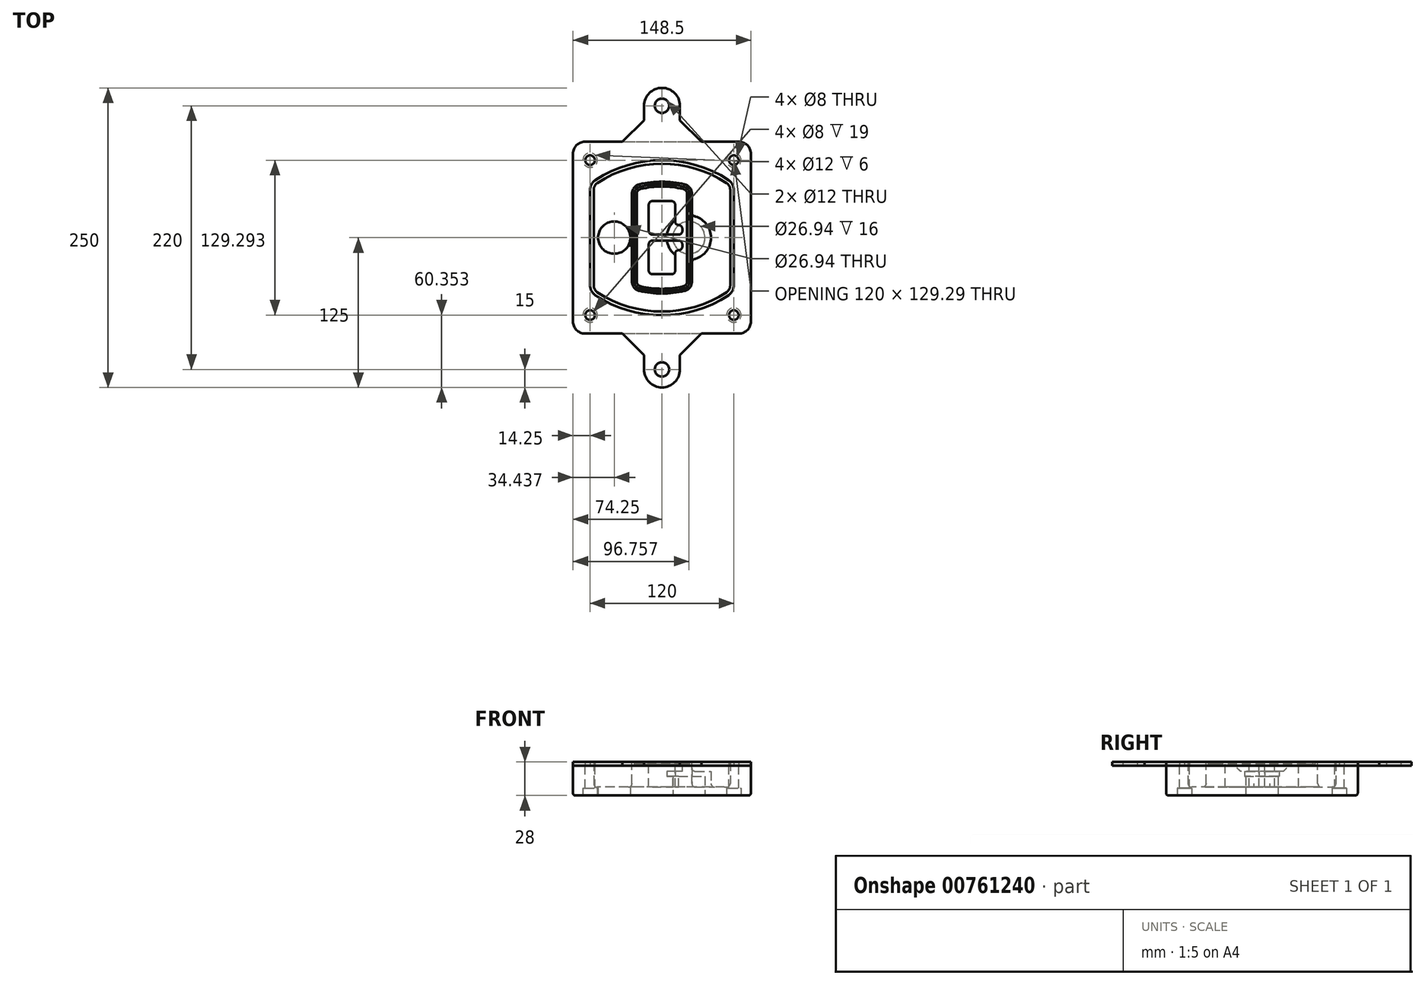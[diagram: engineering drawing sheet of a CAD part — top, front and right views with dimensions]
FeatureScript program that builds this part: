
annotation { "Feature Type Name" : "Feature", "Feature Type Description" : "" }
export const myFeature = defineFeature(function(context is Context, id is Id, definition is map)
    precondition{}
    {
        {
            var Q0;
            Q0=qCreatedBy(makeId("Top.planeOp"),FACE);
            var sketch = newSketch(context, id + "F0", { "sketchPlane" : qUnion([Q0])});
            skPoint(sketch, "E0.rect.middle", {"position": v(0, 0) * mm});
            skLineSegment(sketch, "E1.bottom", {"start": v(-64.25, -80) * mm, "end": v(64.25, -80) * mm});
            skLineSegment(sketch, "E1.top", {"start": v(-64.25, 80) * mm, "end": v(64.25, 80) * mm});
            skLineSegment(sketch, "E1.left", {"start": v(-74.25, -70) * mm, "end": v(-74.25, 70) * mm});
            skLineSegment(sketch, "E1.right", {"start": v(74.25, -70) * mm, "end": v(74.25, 70) * mm});
            skLineSegment(sketch, "E2", {"start": v(-74.25, 80) * mm, "end": v(74.25, -80) * mm, "construction": true});
            skLineSegment(sketch, "E3", {"start": v(74.25, 80) * mm, "end": v(-74.25, -80) * mm, "construction": true});
            skCircle(sketch, "E4", {"center": v(-60, 64.65) * mm, "radius": 4 * mm});
            skCircle(sketch, "E5", {"center": v(60, 64.65) * mm, "radius": 4 * mm});
            skCircle(sketch, "E6", {"center": v(60, -64.65) * mm, "radius": 4 * mm});
            skCircle(sketch, "E7", {"center": v(-60, -64.65) * mm, "radius": 4 * mm});
            skLineSegment(sketch, "E8", {"start": v(-60, 64.65) * mm, "end": v(60, 64.65) * mm, "construction": true});
            skLineSegment(sketch, "E9", {"start": v(60, 64.65) * mm, "end": v(60, -64.65) * mm, "construction": true});
            skLineSegment(sketch, "E10", {"start": v(60, -64.65) * mm, "end": v(-60, -64.65) * mm, "construction": true});
            skLineSegment(sketch, "E11", {"start": v(-60, -64.65) * mm, "end": v(-60, 64.65) * mm, "construction": true});
            skLineSegment(sketch, "E12", {"start": v(-60, 39.77) * mm, "end": v(-60, -39.77) * mm});
            skLineSegment(sketch, "E13", {"start": v(60, 39.77) * mm, "end": v(60, -39.77) * mm});
            skArc(sketch, "E14", {"start": v(55.47, 48.14) * mm, "mid": v(0, 64.65) * mm, "end": v(-55.47, 48.14) * mm});
            skArc(sketch, "E15", {"start": v(-55.47, -48.14) * mm, "mid": v(0, -64.65) * mm, "end": v(55.47, -48.14) * mm});
            skLineSegment(sketch, "E16", {"start": v(-60, 0) * mm, "end": v(60, 0) * mm, "construction": true});
            skPoint(sketch, "E17.visualSharp", {"position": v(-60, -45) * mm});
            skArc(sketch, "E17.filletArc", {"start": v(-60, -39.77) * mm, "mid": v(-58.8, -44.53) * mm, "end": v(-55.47, -48.14) * mm});
            skPoint(sketch, "E18.visualSharp", {"position": v(-60, 45) * mm});
            skArc(sketch, "E18.filletArc", {"start": v(-55.47, 48.14) * mm, "mid": v(-58.8, 44.53) * mm, "end": v(-60, 39.77) * mm});
            skPoint(sketch, "E19.visualSharp", {"position": v(60, 45) * mm});
            skArc(sketch, "E19.filletArc", {"start": v(60, 39.77) * mm, "mid": v(58.8, 44.53) * mm, "end": v(55.47, 48.14) * mm});
            skPoint(sketch, "E20.visualSharp", {"position": v(60, -45) * mm});
            skArc(sketch, "E20.filletArc", {"start": v(55.47, -48.14) * mm, "mid": v(58.8, -44.53) * mm, "end": v(60, -39.77) * mm});
            skPoint(sketch, "E21.visualSharp", {"position": v(-74.25, 80) * mm});
            skArc(sketch, "E21.filletArc", {"start": v(-64.25, 80) * mm, "mid": v(-71.32, 77.07) * mm, "end": v(-74.25, 70) * mm});
            skPoint(sketch, "E22.visualSharp", {"position": v(74.25, 80) * mm});
            skArc(sketch, "E22.filletArc", {"start": v(74.25, 70) * mm, "mid": v(71.32, 77.07) * mm, "end": v(64.25, 80) * mm});
            skPoint(sketch, "E23.visualSharp", {"position": v(74.25, -80) * mm});
            skArc(sketch, "E23.filletArc", {"start": v(64.25, -80) * mm, "mid": v(71.32, -77.07) * mm, "end": v(74.25, -70) * mm});
            skPoint(sketch, "E24.visualSharp", {"position": v(-74.25, -80) * mm});
            skArc(sketch, "E24.filletArc", {"start": v(-74.25, -70) * mm, "mid": v(-71.32, -77.07) * mm, "end": v(-64.25, -80) * mm});
            skArc(sketch, "E25.0", {"start": v(57, 39.77) * mm, "mid": v(56.16, 43.1) * mm, "end": v(53.83, 45.63) * mm});
            skLineSegment(sketch, "E25.1", {"start": v(57, 39.77) * mm, "end": v(57, -39.77) * mm});
            skArc(sketch, "E25.2", {"start": v(53.83, -45.63) * mm, "mid": v(56.16, -43.1) * mm, "end": v(57, -39.77) * mm});
            skArc(sketch, "E25.3", {"start": v(-53.83, -45.63) * mm, "mid": v(0, -61.65) * mm, "end": v(53.83, -45.63) * mm});
            skArc(sketch, "E25.4", {"start": v(-57, -39.77) * mm, "mid": v(-56.16, -43.1) * mm, "end": v(-53.83, -45.63) * mm});
            skArc(sketch, "E25.5", {"start": v(53.83, 45.63) * mm, "mid": v(0, 61.65) * mm, "end": v(-53.83, 45.63) * mm});
            skLineSegment(sketch, "E25.6", {"start": v(-57, 39.77) * mm, "end": v(-57, -39.77) * mm});
            skArc(sketch, "E25.7", {"start": v(-53.83, 45.63) * mm, "mid": v(-56.16, 43.1) * mm, "end": v(-57, 39.77) * mm});
            skArc(sketch, "E26.0", {"start": v(-57.66, 51.49) * mm, "mid": v(-62.31, 46.43) * mm, "end": v(-64, 39.77) * mm});
            skArc(sketch, "E26.1", {"start": v(57.66, 51.49) * mm, "mid": v(0, 68.65) * mm, "end": v(-57.66, 51.49) * mm});
            skArc(sketch, "E26.2", {"start": v(64, 39.77) * mm, "mid": v(62.31, 46.43) * mm, "end": v(57.66, 51.49) * mm});
            skLineSegment(sketch, "E26.3", {"start": v(64, 39.77) * mm, "end": v(64, -39.77) * mm});
            skArc(sketch, "E26.4", {"start": v(57.66, -51.49) * mm, "mid": v(62.31, -46.43) * mm, "end": v(64, -39.77) * mm});
            skLineSegment(sketch, "E26.5", {"start": v(-64, 39.77) * mm, "end": v(-64, -39.77) * mm});
            skArc(sketch, "E26.6", {"start": v(-57.66, -51.49) * mm, "mid": v(0, -68.65) * mm, "end": v(57.66, -51.49) * mm});
            skArc(sketch, "E26.7", {"start": v(-64, -39.77) * mm, "mid": v(-62.31, -46.43) * mm, "end": v(-57.66, -51.49) * mm});
            skSolve(sketch);
        }
        {
            var Q0;
            Q0=makeQuery(id+"F0.imprint","IMPRINT",FACE,{"disambiguationData":[TD([[makeQuery(id+"F0.imprint","IMPRINT",EDGE,{"derivedFrom":sQuery(id+"F0.wireOp",EDGE,"E1.bottom")}),1.0]])]});
            var Q1;
            Q1=makeQuery(id+"F0.imprint","IMPRINT",FACE,{"disambiguationData":[TD([[makeQuery(id+"F0.imprint","IMPRINT",EDGE,{"derivedFrom":sQuery(id+"F0.wireOp",EDGE,"E12")}),1.0]])]});
            var Q2;
            Q2=makeQuery(id+"F0.imprint","IMPRINT",FACE,{"disambiguationData":[TD([[makeQuery(id+"F0.imprint","IMPRINT",EDGE,{"derivedFrom":sQuery(id+"F0.wireOp",EDGE,"E25.0")}),1.0]])]});
            var Q3;
            Q3=makeQuery(id+"F0.imprint","IMPRINT",FACE,{"disambiguationData":[TD([[makeQuery(id+"F0.imprint","IMPRINT",EDGE,{"derivedFrom":sQuery(id+"F0.wireOp",EDGE,"E12")}),-1.0]])]});
            extrude(context, id + "F1", {"entities" : qUnion([Q0, Q1, Q2, Q3]), "oppositeDirection" : true, "depth" : 25 * mm});
        }
        {
            var Q0;
            Q0=makeQuery(id+"F0.imprint","IMPRINT",FACE,{"disambiguationData":[TD([[makeQuery(id+"F0.imprint","IMPRINT",EDGE,{"derivedFrom":sQuery(id+"F0.wireOp",EDGE,"E12")}),1.0]])]});
            extrude(context, id + "F2", {"entities" : qUnion([Q0]), "operationType" : NewBodyOperationType.ADD, "depth" : 3 * mm});
        }
        {
            var Q0;
            Q0=makeQuery(id+"F0.imprint","IMPRINT",FACE,{"disambiguationData":[TD([[makeQuery(id+"F0.imprint","IMPRINT",EDGE,{"derivedFrom":sQuery(id+"F0.wireOp",EDGE,"E25.0")}),1.0]])]});
            extrude(context, id + "F3", {"entities" : qUnion([Q0]), "operationType" : NewBodyOperationType.REMOVE, "oppositeDirection" : true, "depth" : 18 * mm});
        }
        {
            var Q0;
            Q0=makeQuery(id+"F2.opExtrude","CAP_FACE",FACE,{"disambiguationData":[OSD([sQuery(id+"F0.wireOp",EDGE,"E12"),sQuery(id+"F0.wireOp",EDGE,"E13"),sQuery(id+"F0.wireOp",EDGE,"E14"),sQuery(id+"F0.wireOp",EDGE,"E15"),sQuery(id+"F0.wireOp",EDGE,"E17.filletArc"),sQuery(id+"F0.wireOp",EDGE,"E18.filletArc"),sQuery(id+"F0.wireOp",EDGE,"E19.filletArc"),sQuery(id+"F0.wireOp",EDGE,"E20.filletArc"),sQuery(id+"F0.wireOp",EDGE,"E25.0"),sQuery(id+"F0.wireOp",EDGE,"E25.1"),sQuery(id+"F0.wireOp",EDGE,"E25.2"),sQuery(id+"F0.wireOp",EDGE,"E25.3"),sQuery(id+"F0.wireOp",EDGE,"E25.4"),sQuery(id+"F0.wireOp",EDGE,"E25.5"),sQuery(id+"F0.wireOp",EDGE,"E25.6"),sQuery(id+"F0.wireOp",EDGE,"E25.7")])],"isStart":false});
            var sketch = newSketch(context, id + "F4", { "sketchPlane" : qUnion([Q0])});
            skArc(sketch, "E27.0", {"start": v(-18.8, -44.5) * mm, "mid": v(0, -46.65) * mm, "end": v(18.8, -44.5) * mm});
            skArc(sketch, "E28.0", {"start": v(18.8, 44.5) * mm, "mid": v(0, 46.65) * mm, "end": v(-18.8, 44.5) * mm});
            skLineSegment(sketch, "E29", {"start": v(-25, 36.7) * mm, "end": v(-25, -36.7) * mm});
            skLineSegment(sketch, "E30", {"start": v(25, 36.7) * mm, "end": v(25, -36.7) * mm});
            skLineSegment(sketch, "E31", {"start": v(-25, 42.81) * mm, "end": v(25, 42.81) * mm, "construction": true});
            skLineSegment(sketch, "E32", {"start": v(-25, -42.81) * mm, "end": v(25, -42.81) * mm, "construction": true});
            skPoint(sketch, "E33.visualSharp", {"position": v(-25, 42.81) * mm});
            skArc(sketch, "E33.filletArc", {"start": v(-18.8, 44.5) * mm, "mid": v(-23.26, 41.69) * mm, "end": v(-25, 36.7) * mm});
            skPoint(sketch, "E34.visualSharp", {"position": v(25, 42.81) * mm});
            skArc(sketch, "E34.filletArc", {"start": v(25, 36.7) * mm, "mid": v(23.26, 41.69) * mm, "end": v(18.8, 44.5) * mm});
            skPoint(sketch, "E35.visualSharp", {"position": v(25, -42.81) * mm});
            skArc(sketch, "E35.filletArc", {"start": v(18.8, -44.5) * mm, "mid": v(23.26, -41.69) * mm, "end": v(25, -36.7) * mm});
            skPoint(sketch, "E36.visualSharp", {"position": v(-25, -42.81) * mm});
            skArc(sketch, "E36.filletArc", {"start": v(-25, -36.7) * mm, "mid": v(-23.26, -41.69) * mm, "end": v(-18.8, -44.5) * mm});
            skArc(sketch, "E37.0", {"start": v(53.83, 45.63) * mm, "mid": v(0, 61.65) * mm, "end": v(-53.83, 45.63) * mm});
            skArc(sketch, "E37.1", {"start": v(-53.83, 45.63) * mm, "mid": v(-56.16, 43.1) * mm, "end": v(-57, 39.77) * mm});
            skLineSegment(sketch, "E37.2", {"start": v(-57, 39.77) * mm, "end": v(-57, -39.77) * mm});
            skArc(sketch, "E37.3", {"start": v(-57, -39.77) * mm, "mid": v(-56.16, -43.1) * mm, "end": v(-53.83, -45.63) * mm});
            skArc(sketch, "E37.4", {"start": v(-53.83, -45.63) * mm, "mid": v(0, -61.65) * mm, "end": v(53.83, -45.63) * mm});
            skArc(sketch, "E37.5", {"start": v(53.83, -45.63) * mm, "mid": v(56.16, -43.1) * mm, "end": v(57, -39.77) * mm});
            skLineSegment(sketch, "E37.6", {"start": v(57, 39.77) * mm, "end": v(57, -39.77) * mm});
            skArc(sketch, "E37.7", {"start": v(57, 39.77) * mm, "mid": v(56.16, 43.1) * mm, "end": v(53.83, 45.63) * mm});
            skLineSegment(sketch, "E38.0", {"start": v(23, 36.7) * mm, "end": v(23, -36.7) * mm});
            skArc(sketch, "E38.1", {"start": v(18.35, -42.55) * mm, "mid": v(21.7, -40.44) * mm, "end": v(23, -36.7) * mm});
            skArc(sketch, "E38.2", {"start": v(-18.35, -42.55) * mm, "mid": v(0, -44.65) * mm, "end": v(18.35, -42.55) * mm});
            skArc(sketch, "E38.3", {"start": v(-23, -36.7) * mm, "mid": v(-21.7, -40.44) * mm, "end": v(-18.35, -42.55) * mm});
            skLineSegment(sketch, "E38.4", {"start": v(-23, 36.7) * mm, "end": v(-23, -36.7) * mm});
            skArc(sketch, "E38.5", {"start": v(23, 36.7) * mm, "mid": v(21.7, 40.44) * mm, "end": v(18.35, 42.55) * mm});
            skArc(sketch, "E38.6", {"start": v(-18.35, 42.55) * mm, "mid": v(-21.7, 40.44) * mm, "end": v(-23, 36.7) * mm});
            skArc(sketch, "E38.7", {"start": v(18.35, 42.55) * mm, "mid": v(0, 44.65) * mm, "end": v(-18.35, 42.55) * mm});
            skArc(sketch, "E39.0", {"start": v(21, 36.7) * mm, "mid": v(20.13, 39.2) * mm, "end": v(17.9, 40.6) * mm});
            skLineSegment(sketch, "E39.1", {"start": v(21, 36.7) * mm, "end": v(21, -36.7) * mm});
            skArc(sketch, "E39.2", {"start": v(17.9, -40.6) * mm, "mid": v(20.13, -39.2) * mm, "end": v(21, -36.7) * mm});
            skArc(sketch, "E39.3", {"start": v(-17.9, -40.6) * mm, "mid": v(0, -42.65) * mm, "end": v(17.9, -40.6) * mm});
            skArc(sketch, "E39.4", {"start": v(-21, -36.7) * mm, "mid": v(-20.13, -39.2) * mm, "end": v(-17.9, -40.6) * mm});
            skArc(sketch, "E39.5", {"start": v(17.9, 40.6) * mm, "mid": v(0, 42.65) * mm, "end": v(-17.9, 40.6) * mm});
            skLineSegment(sketch, "E39.6", {"start": v(-21, 36.7) * mm, "end": v(-21, -36.7) * mm});
            skArc(sketch, "E39.7", {"start": v(-17.9, 40.6) * mm, "mid": v(-20.13, 39.2) * mm, "end": v(-21, 36.7) * mm});
            skLineSegment(sketch, "E40", {"start": v(-25, 0) * mm, "end": v(25, 0) * mm, "construction": true});
            skLineSegment(sketch, "E41", {"start": v(-11, 5.5) * mm, "end": v(-11, 27.5) * mm});
            skLineSegment(sketch, "E42", {"start": v(-8, 30.5) * mm, "end": v(8, 30.5) * mm});
            skLineSegment(sketch, "E43", {"start": v(11, 27.5) * mm, "end": v(11, 13.5) * mm});
            skLineSegment(sketch, "E44", {"start": v(14, 10.5) * mm, "end": v(14, 10.5) * mm});
            skLineSegment(sketch, "E45", {"start": v(17, 7.5) * mm, "end": v(17, 5.5) * mm});
            skLineSegment(sketch, "E46", {"start": v(14, 2.5) * mm, "end": v(-8, 2.5) * mm});
            skPoint(sketch, "E47.visualSharp", {"position": v(-11, 30.5) * mm});
            skArc(sketch, "E47.filletArc", {"start": v(-8, 30.5) * mm, "mid": v(-10.12, 29.62) * mm, "end": v(-11, 27.5) * mm});
            skPoint(sketch, "E48.visualSharp", {"position": v(11, 30.5) * mm});
            skArc(sketch, "E48.filletArc", {"start": v(11, 27.5) * mm, "mid": v(10.12, 29.62) * mm, "end": v(8, 30.5) * mm});
            skPoint(sketch, "E49.visualSharp", {"position": v(11, 10.5) * mm});
            skArc(sketch, "E49.filletArc", {"start": v(11, 13.5) * mm, "mid": v(11.88, 11.38) * mm, "end": v(14, 10.5) * mm});
            skPoint(sketch, "E50.visualSharp", {"position": v(17, 10.5) * mm});
            skArc(sketch, "E50.filletArc", {"start": v(17, 7.5) * mm, "mid": v(16.12, 9.62) * mm, "end": v(14, 10.5) * mm});
            skPoint(sketch, "E51.visualSharp", {"position": v(17, 2.5) * mm});
            skArc(sketch, "E51.filletArc", {"start": v(14, 2.5) * mm, "mid": v(16.12, 3.38) * mm, "end": v(17, 5.5) * mm});
            skPoint(sketch, "E52.visualSharp", {"position": v(-11, 2.5) * mm});
            skArc(sketch, "E52.filletArc", {"start": v(-11, 5.5) * mm, "mid": v(-10.12, 3.38) * mm, "end": v(-8, 2.5) * mm});
            skLineSegment(sketch, "E53.0.MirrorCS", {"start": v(14, -2.5) * mm, "end": v(-8, -2.5) * mm});
            skArc(sketch, "E54.0.MirrorCS", {"start": v(-11, -5.5) * mm, "mid": v(-10.12, -3.38) * mm, "end": v(-8, -2.5) * mm});
            skLineSegment(sketch, "E55.0.MirrorCS", {"start": v(-11, -5.5) * mm, "end": v(-11, -27.5) * mm});
            skArc(sketch, "E56.0.MirrorCS", {"start": v(-8, -30.5) * mm, "mid": v(-10.12, -29.62) * mm, "end": v(-11, -27.5) * mm});
            skLineSegment(sketch, "E57.0.MirrorCS", {"start": v(-8, -30.5) * mm, "end": v(8, -30.5) * mm});
            skArc(sketch, "E58.0.MirrorCS", {"start": v(11, -27.5) * mm, "mid": v(10.12, -29.62) * mm, "end": v(8, -30.5) * mm});
            skLineSegment(sketch, "E59.0.MirrorCS", {"start": v(11, -27.5) * mm, "end": v(11, -13.5) * mm});
            skArc(sketch, "E60.0.MirrorCS", {"start": v(11, -13.5) * mm, "mid": v(11.88, -11.38) * mm, "end": v(14, -10.5) * mm});
            skArc(sketch, "E61.0.MirrorCS", {"start": v(17, -7.5) * mm, "mid": v(16.12, -9.62) * mm, "end": v(14, -10.5) * mm});
            skLineSegment(sketch, "E62.0.MirrorCS", {"start": v(17, -7.5) * mm, "end": v(17, -5.5) * mm});
            skArc(sketch, "E63.0.MirrorCS", {"start": v(14, -2.5) * mm, "mid": v(16.12, -3.38) * mm, "end": v(17, -5.5) * mm});
            skSolve(sketch);
        }
        {
            var Q0;
            Q0=makeQuery(id+"F4.imprint","IMPRINT",FACE,{"disambiguationData":[TD([[makeQuery(id+"F4.imprint","IMPRINT",EDGE,{"derivedFrom":sQuery(id+"F4.wireOp",EDGE,"E27.0")}),1.0]])]});
            var Q1;
            Q1=makeQuery(id+"F4.imprint","IMPRINT",FACE,{"disambiguationData":[TD([[makeQuery(id+"F4.imprint","IMPRINT",EDGE,{"derivedFrom":sQuery(id+"F4.wireOp",EDGE,"E38.0")}),-1.0]])]});
            var Q2;
            Q2=makeQuery(id+"F4.imprint","IMPRINT",FACE,{"disambiguationData":[TD([[makeQuery(id+"F4.imprint","IMPRINT",EDGE,{"derivedFrom":sQuery(id+"F4.wireOp",EDGE,"E39.0")}),1.0]])]});
            extrude(context, id + "F5", {"entities" : qUnion([Q0, Q1, Q2]), "operationType" : NewBodyOperationType.ADD, "endBound" : BoundingType.UP_TO_NEXT, "oppositeDirection" : true, "depth" : 25 * mm});
        }
        {
            var Q0;
            Q0=makeQuery(id+"F4.imprint","IMPRINT",FACE,{"disambiguationData":[TD([[makeQuery(id+"F4.imprint","IMPRINT",EDGE,{"derivedFrom":sQuery(id+"F4.wireOp",EDGE,"E38.0")}),-1.0]])]});
            extrude(context, id + "F6", {"entities" : qUnion([Q0]), "operationType" : NewBodyOperationType.REMOVE, "oppositeDirection" : true, "depth" : 2 * mm});
        }
        {
            var Q0;
            Q0=makeQuery(id+"F1.opExtrude","CAP_FACE",FACE,{"disambiguationData":[OSD([sQuery(id+"F0.wireOp",EDGE,"E1.bottom"),sQuery(id+"F0.wireOp",EDGE,"E1.top"),sQuery(id+"F0.wireOp",EDGE,"E1.left"),sQuery(id+"F0.wireOp",EDGE,"E1.right"),sQuery(id+"F0.wireOp",EDGE,"E4"),sQuery(id+"F0.wireOp",EDGE,"E5"),sQuery(id+"F0.wireOp",EDGE,"E6"),sQuery(id+"F0.wireOp",EDGE,"E7"),sQuery(id+"F0.wireOp",EDGE,"E21.filletArc"),sQuery(id+"F0.wireOp",EDGE,"E22.filletArc"),sQuery(id+"F0.wireOp",EDGE,"E23.filletArc"),sQuery(id+"F0.wireOp",EDGE,"E24.filletArc")])],"isStart":false});
            var sketch = newSketch(context, id + "F7", { "sketchPlane" : qUnion([Q0])});
            skCircle(sketch, "E64", {"center": v(22.5, 0) * mm, "radius": 13.47 * mm});
            skCircle(sketch, "E65", {"center": v(-39.81, 0) * mm, "radius": 13.47 * mm});
            skLineSegment(sketch, "E66", {"start": v(74.25, 0) * mm, "end": v(-74.25, 0) * mm});
            skCircle(sketch, "E67", {"center": v(22.5, 0) * mm, "radius": 18.47 * mm});
            skCircle(sketch, "E68", {"center": v(60, -64.65) * mm, "radius": 6 * mm});
            skCircle(sketch, "E69", {"center": v(-60, -64.65) * mm, "radius": 6 * mm});
            skCircle(sketch, "E70", {"center": v(-60, 64.65) * mm, "radius": 6 * mm});
            skCircle(sketch, "E71", {"center": v(60, 64.65) * mm, "radius": 6 * mm});
            skSolve(sketch);
        }
        {
            var Q0;
            {var subQ1=sQuery(id+"F7.wireOp",EDGE,"E66");var subQ4=sQuery(id+"F7.wireOp",EDGE,"E64");var subQ6=makeQuery(id+"F7.imprint","INTERSECT",VERTEX,{"disambiguationData":[OD(0.0)],"derivedFrom":[subQ4,subQ1]});Q0=makeQuery(id+"F7.imprint","IMPRINT",FACE,{"disambiguationData":[TD([[makeQuery(id+"F7.imprint","IMPRINT",EDGE,{"disambiguationData":[TD([[subQ6,-1.0]])],"derivedFrom":subQ4}),-1.0]])]});}
            var Q1;
            {var subQ0=sQuery(id+"F7.wireOp",EDGE,"E66");var subQ1=sQuery(id+"F7.wireOp",EDGE,"E64");var subQ3=makeQuery(id+"F7.imprint","INTERSECT",VERTEX,{"disambiguationData":[OD(0.0)],"derivedFrom":[subQ1,subQ0]});Q1=makeQuery(id+"F7.imprint","IMPRINT",FACE,{"disambiguationData":[TD([[makeQuery(id+"F7.imprint","IMPRINT",EDGE,{"disambiguationData":[TD([[subQ3,-1.0]])],"derivedFrom":subQ1}),1.0]])]});}
            var Q2;
            {var subQ0=sQuery(id+"F7.wireOp",EDGE,"E66");var subQ1=sQuery(id+"F7.wireOp",EDGE,"E64");var subQ3=makeQuery(id+"F7.imprint","INTERSECT",VERTEX,{"disambiguationData":[OD(0.0)],"derivedFrom":[subQ1,subQ0]});Q2=makeQuery(id+"F7.imprint","IMPRINT",FACE,{"disambiguationData":[TD([[makeQuery(id+"F7.imprint","IMPRINT",EDGE,{"disambiguationData":[TD([[subQ3,1.0]])],"derivedFrom":subQ1}),1.0]])]});}
            var Q3;
            {var subQ1=sQuery(id+"F7.wireOp",EDGE,"E66");var subQ4=sQuery(id+"F7.wireOp",EDGE,"E64");var subQ6=makeQuery(id+"F7.imprint","INTERSECT",VERTEX,{"disambiguationData":[OD(0.0)],"derivedFrom":[subQ4,subQ1]});Q3=makeQuery(id+"F7.imprint","IMPRINT",FACE,{"disambiguationData":[TD([[makeQuery(id+"F7.imprint","IMPRINT",EDGE,{"disambiguationData":[TD([[subQ6,1.0]])],"derivedFrom":subQ4}),-1.0]])]});}
            extrude(context, id + "F8", {"entities" : qUnion([Q0, Q1, Q2, Q3]), "operationType" : NewBodyOperationType.ADD, "oppositeDirection" : true, "depth" : 20 * mm});
        }
        {
            var Q0;
            {var subQ0=sQuery(id+"F7.wireOp",EDGE,"E66");var subQ1=sQuery(id+"F7.wireOp",EDGE,"E64");var subQ3=makeQuery(id+"F7.imprint","INTERSECT",VERTEX,{"disambiguationData":[OD(0.0)],"derivedFrom":[subQ1,subQ0]});Q0=makeQuery(id+"F7.imprint","IMPRINT",FACE,{"disambiguationData":[TD([[makeQuery(id+"F7.imprint","IMPRINT",EDGE,{"disambiguationData":[TD([[subQ3,-1.0]])],"derivedFrom":subQ1}),1.0]])]});}
            var Q1;
            {var subQ0=sQuery(id+"F7.wireOp",EDGE,"E66");var subQ1=sQuery(id+"F7.wireOp",EDGE,"E64");var subQ3=makeQuery(id+"F7.imprint","INTERSECT",VERTEX,{"disambiguationData":[OD(0.0)],"derivedFrom":[subQ1,subQ0]});Q1=makeQuery(id+"F7.imprint","IMPRINT",FACE,{"disambiguationData":[TD([[makeQuery(id+"F7.imprint","IMPRINT",EDGE,{"disambiguationData":[TD([[subQ3,1.0]])],"derivedFrom":subQ1}),1.0]])]});}
            extrude(context, id + "F9", {"entities" : qUnion([Q0, Q1]), "operationType" : NewBodyOperationType.REMOVE, "oppositeDirection" : true, "depth" : 16 * mm});
        }
        {
            var Q0;
            {var subQ0=sQuery(id+"F7.wireOp",EDGE,"E66");var subQ1=sQuery(id+"F7.wireOp",EDGE,"E65");var subQ3=makeQuery(id+"F7.imprint","INTERSECT",VERTEX,{"disambiguationData":[OD(0.0)],"derivedFrom":[subQ1,subQ0]});Q0=makeQuery(id+"F7.imprint","IMPRINT",FACE,{"disambiguationData":[TD([[makeQuery(id+"F7.imprint","IMPRINT",EDGE,{"disambiguationData":[TD([[subQ3,-1.0]])],"derivedFrom":subQ1}),1.0]])]});}
            var Q1;
            {var subQ0=sQuery(id+"F7.wireOp",EDGE,"E66");var subQ1=sQuery(id+"F7.wireOp",EDGE,"E65");var subQ3=makeQuery(id+"F7.imprint","INTERSECT",VERTEX,{"disambiguationData":[OD(0.0)],"derivedFrom":[subQ1,subQ0]});Q1=makeQuery(id+"F7.imprint","IMPRINT",FACE,{"disambiguationData":[TD([[makeQuery(id+"F7.imprint","IMPRINT",EDGE,{"disambiguationData":[TD([[subQ3,1.0]])],"derivedFrom":subQ1}),1.0]])]});}
            extrude(context, id + "F10", {"entities" : qUnion([Q0, Q1]), "operationType" : NewBodyOperationType.REMOVE, "oppositeDirection" : true, "depth" : 25 * mm});
        }
        {
            var Q0;
            Q0=makeQuery(id+"F7.imprint","IMPRINT",FACE,{"disambiguationData":[TD([[makeQuery(id+"F7.imprint","IMPRINT",EDGE,{"derivedFrom":sQuery(id+"F7.wireOp",EDGE,"E68")}),1.0]])]});
            var Q1;
            Q1=makeQuery(id+"F7.imprint","IMPRINT",FACE,{"disambiguationData":[TD([[makeQuery(id+"F7.imprint","IMPRINT",EDGE,{"derivedFrom":makeQuery(id+"F1.opExtrude","CAP_EDGE",EDGE,{"disambiguationData":[OSD([sQuery(id+"F0.wireOp",EDGE,"E5")])],"isStart":false})}),-1.0]])]});
            var Q2;
            Q2=makeQuery(id+"F7.imprint","IMPRINT",FACE,{"disambiguationData":[TD([[makeQuery(id+"F7.imprint","IMPRINT",EDGE,{"derivedFrom":sQuery(id+"F7.wireOp",EDGE,"E69")}),1.0]])]});
            var Q3;
            Q3=makeQuery(id+"F7.imprint","IMPRINT",FACE,{"disambiguationData":[TD([[makeQuery(id+"F7.imprint","IMPRINT",EDGE,{"derivedFrom":makeQuery(id+"F1.opExtrude","CAP_EDGE",EDGE,{"disambiguationData":[OSD([sQuery(id+"F0.wireOp",EDGE,"E4")])],"isStart":false})}),-1.0]])]});
            var Q4;
            Q4=makeQuery(id+"F7.imprint","IMPRINT",FACE,{"disambiguationData":[TD([[makeQuery(id+"F7.imprint","IMPRINT",EDGE,{"derivedFrom":sQuery(id+"F7.wireOp",EDGE,"E70")}),1.0]])]});
            var Q5;
            Q5=makeQuery(id+"F7.imprint","IMPRINT",FACE,{"disambiguationData":[TD([[makeQuery(id+"F7.imprint","IMPRINT",EDGE,{"derivedFrom":makeQuery(id+"F1.opExtrude","CAP_EDGE",EDGE,{"disambiguationData":[OSD([sQuery(id+"F0.wireOp",EDGE,"E7")])],"isStart":false})}),-1.0]])]});
            var Q6;
            Q6=makeQuery(id+"F7.imprint","IMPRINT",FACE,{"disambiguationData":[TD([[makeQuery(id+"F7.imprint","IMPRINT",EDGE,{"derivedFrom":sQuery(id+"F7.wireOp",EDGE,"E71")}),1.0]])]});
            var Q7;
            Q7=makeQuery(id+"F7.imprint","IMPRINT",FACE,{"disambiguationData":[TD([[makeQuery(id+"F7.imprint","IMPRINT",EDGE,{"derivedFrom":makeQuery(id+"F1.opExtrude","CAP_EDGE",EDGE,{"disambiguationData":[OSD([sQuery(id+"F0.wireOp",EDGE,"E6")])],"isStart":false})}),-1.0]])]});
            extrude(context, id + "F11", {"entities" : qUnion([Q0, Q1, Q2, Q3, Q4, Q5, Q6, Q7]), "operationType" : NewBodyOperationType.REMOVE, "oppositeDirection" : true, "depth" : 6 * mm});
        }
        {
            var Q0;
            Q0=makeQuery(id+"F9.boolean.opBoolean","COPY",FACE,{"derivedFrom":makeQuery(id+"F9.opExtrude","CAP_FACE",FACE,{"disambiguationData":[OSD([sQuery(id+"F7.wireOp",EDGE,"E64")])],"isStart":false})});
            var sketch = newSketch(context, id + "F12", { "sketchPlane" : qUnion([Q0])});
            skArc(sketch, "E72.0", {"start": v(11, 14.45) * mm, "mid": v(6.45, 9.13) * mm, "end": v(4.2, 2.5) * mm});
            skArc(sketch, "E72.1", {"start": v(4.2, -2.5) * mm, "mid": v(6.45, -9.13) * mm, "end": v(11, -14.45) * mm});
            skLineSegment(sketch, "E73", {"start": v(4.2, -2.5) * mm, "end": v(14, -2.5) * mm});
            skLineSegment(sketch, "E74.0", {"start": v(14, 2.5) * mm, "end": v(4.2, 2.5) * mm});
            skArc(sketch, "E74.1", {"start": v(14, 2.5) * mm, "mid": v(16.12, 3.38) * mm, "end": v(17, 5.5) * mm});
            skLineSegment(sketch, "E74.2", {"start": v(17, 7.5) * mm, "end": v(17, 5.5) * mm});
            skArc(sketch, "E74.3", {"start": v(17, 7.5) * mm, "mid": v(16.12, 9.62) * mm, "end": v(14, 10.5) * mm});
            skArc(sketch, "E74.4", {"start": v(11, 13.5) * mm, "mid": v(11.88, 11.38) * mm, "end": v(14, 10.5) * mm});
            skLineSegment(sketch, "E74.5", {"start": v(11, 14.45) * mm, "end": v(11, 13.5) * mm});
            skLineSegment(sketch, "E74.7", {"start": v(14, -2.5) * mm, "end": v(4.2, -2.5) * mm});
            skArc(sketch, "E74.8", {"start": v(14, -2.5) * mm, "mid": v(16.12, -3.38) * mm, "end": v(17, -5.5) * mm});
            skLineSegment(sketch, "E74.9", {"start": v(17, -7.5) * mm, "end": v(17, -5.5) * mm});
            skArc(sketch, "E74.10", {"start": v(17, -7.5) * mm, "mid": v(16.12, -9.62) * mm, "end": v(14, -10.5) * mm});
            skArc(sketch, "E74.11", {"start": v(11, -13.5) * mm, "mid": v(11.88, -11.38) * mm, "end": v(14, -10.5) * mm});
            skLineSegment(sketch, "E74.12", {"start": v(11, -14.45) * mm, "end": v(11, -13.5) * mm});
            skPoint(sketch, "E75.orphan", {"position": v(11, -27.5) * mm});
            skPoint(sketch, "E76.orphan", {"position": v(-8, -2.5) * mm});
            skPoint(sketch, "E77.orphan", {"position": v(-8, 2.5) * mm});
            skPoint(sketch, "E78.orphan", {"position": v(11, 27.5) * mm});
            skSolve(sketch);
        }
        {
            var Q0;
            {var subQ7=sQuery(id+"F12.wireOp",EDGE,"E72.0");var subQ14=sQuery(id+"F12.wireOp",EDGE,"E72.1");var subQ16=sQuery(id+"F12.wireOp",EDGE,"E74.1");var subQ18=sQuery(id+"F12.wireOp",EDGE,"E74.8");Q0=qUnion([makeQuery(id+"F12.imprint","IMPRINT",FACE,{"disambiguationData":[TD([[makeQuery(id+"F12.imprint","IMPRINT",EDGE,{"derivedFrom":subQ7}),1.0]])]}),makeQuery(id+"F12.imprint","IMPRINT",FACE,{"disambiguationData":[TD([[makeQuery(id+"F12.imprint","IMPRINT",EDGE,{"derivedFrom":subQ14}),1.0]])]}),makeQuery(id+"F12.imprint","IMPRINT",FACE,{"disambiguationData":[TD([[makeQuery(id+"F12.imprint","IMPRINT",EDGE,{"derivedFrom":subQ16}),1.0]])]}),makeQuery(id+"F12.imprint","IMPRINT",FACE,{"disambiguationData":[TD([[makeQuery(id+"F12.imprint","IMPRINT",EDGE,{"derivedFrom":subQ18}),-1.0]])]})]);}
            var Q1;
            Q1=makeQuery(id+"F5.boolean.opBoolean","SPLIT",FACE,{"disambiguationData":[TD([makeQuery(id+"F5.opExtrude","SWEPT_FACE",FACE,{"disambiguationData":[OSD([sQuery(id+"F4.wireOp",EDGE,"E41")])]})])],"derivedFrom":makeQuery(id+"F3.boolean.opBoolean","COPY",FACE,{"derivedFrom":makeQuery(id+"F3.opExtrude","CAP_FACE",FACE,{"disambiguationData":[OSD([sQuery(id+"F0.wireOp",EDGE,"E25.0"),sQuery(id+"F0.wireOp",EDGE,"E25.1"),sQuery(id+"F0.wireOp",EDGE,"E25.2"),sQuery(id+"F0.wireOp",EDGE,"E25.3"),sQuery(id+"F0.wireOp",EDGE,"E25.4"),sQuery(id+"F0.wireOp",EDGE,"E25.5"),sQuery(id+"F0.wireOp",EDGE,"E25.6"),sQuery(id+"F0.wireOp",EDGE,"E25.7")])],"isStart":false})})});
            extrude(context, id + "F13", {"entities" : qUnion([Q0]), "operationType" : NewBodyOperationType.REMOVE, "endBound" : BoundingType.UP_TO_SURFACE, "endBoundEntityFace" : qUnion([Q1]), "depth" : 25 * mm});
        }
        {
            var Q0;
            Q0=makeQuery(id+"F3.boolean.opBoolean","COPY",EDGE,{"derivedFrom":makeQuery(id+"F3.opExtrude","CAP_EDGE",EDGE,{"disambiguationData":[OSD([sQuery(id+"F0.wireOp",EDGE,"E25.6")])],"isStart":false})});
            var Q1;
            Q1=makeQuery(id+"F8.boolean.opBoolean","INTERSECT",EDGE,{"derivedFrom":[makeQuery(id+"F5.opExtrude","SWEPT_FACE",FACE,{"disambiguationData":[OSD([sQuery(id+"F4.wireOp",EDGE,"E30")])]}),makeQuery(id+"F8.opExtrude","CAP_FACE",FACE,{"disambiguationData":[OSD([sQuery(id+"F7.wireOp",EDGE,"E67")])],"isStart":false})]});
            var Q2;
            Q2=makeQuery(id+"F8.boolean.opBoolean","INTERSECT",EDGE,{"disambiguationData":[OD(1.0)],"derivedFrom":[makeQuery(id+"F5.opExtrude","SWEPT_FACE",FACE,{"disambiguationData":[OSD([sQuery(id+"F4.wireOp",EDGE,"E30")])]}),makeQuery(id+"F8.opExtrude","SWEPT_FACE",FACE,{"disambiguationData":[OSD([sQuery(id+"F7.wireOp",EDGE,"E67")])]})]});
            var Q3;
            {var subQ0=sQuery(id+"F4.wireOp",EDGE,"E30");Q3=makeQuery(id+"F8.boolean.opBoolean","SPLIT",EDGE,{"disambiguationData":[TD([makeQuery(id+"F5.opExtrude","SWEPT_FACE",FACE,{"disambiguationData":[OSD([sQuery(id+"F4.wireOp",EDGE,"E35.filletArc")])]})])],"derivedFrom":makeQuery(id+"F5.opExtrude","CAP_EDGE",EDGE,{"disambiguationData":[OSD([subQ0])],"isStart":false})});}
            var Q4;
            {var subQ0=sQuery(id+"F0.wireOp",EDGE,"E25.7");var subQ1=sQuery(id+"F0.wireOp",EDGE,"E25.1");var subQ2=sQuery(id+"F0.wireOp",EDGE,"E25.6");var subQ3=sQuery(id+"F0.wireOp",EDGE,"E25.5");var subQ4=sQuery(id+"F0.wireOp",EDGE,"E25.4");var subQ5=sQuery(id+"F0.wireOp",EDGE,"E25.0");var subQ6=sQuery(id+"F0.wireOp",EDGE,"E25.2");var subQ7=sQuery(id+"F0.wireOp",EDGE,"E25.3");Q4=makeQuery(id+"F8.boolean.opBoolean","INTERSECT",EDGE,{"derivedFrom":[makeQuery(id+"F5.boolean.opBoolean","SPLIT",FACE,{"disambiguationData":[TD([makeQuery(id+"F2.opExtrude","SWEPT_FACE",FACE,{"disambiguationData":[OSD([subQ5])]})])],"derivedFrom":makeQuery(id+"F3.boolean.opBoolean","COPY",FACE,{"derivedFrom":makeQuery(id+"F3.opExtrude","CAP_FACE",FACE,{"disambiguationData":[OSD([subQ5,subQ1,subQ6,subQ7,subQ4,subQ3,subQ2,subQ0])],"isStart":false})})}),makeQuery(id+"F8.opExtrude","SWEPT_FACE",FACE,{"disambiguationData":[OSD([sQuery(id+"F7.wireOp",EDGE,"E67")])]})]});}
            var Q5;
            Q5=makeQuery(id+"F8.boolean.opBoolean","INTERSECT",EDGE,{"disambiguationData":[OD(0.0)],"derivedFrom":[makeQuery(id+"F5.opExtrude","SWEPT_FACE",FACE,{"disambiguationData":[OSD([sQuery(id+"F4.wireOp",EDGE,"E30")])]}),makeQuery(id+"F8.opExtrude","SWEPT_FACE",FACE,{"disambiguationData":[OSD([sQuery(id+"F7.wireOp",EDGE,"E67")])]})]});
            fillet(context, id + "F14", {"entities" : qUnion([Q0, Q1, Q2, Q3, Q4, Q5]), "radius" : 3 * mm, "tangentPropagation" : true, "allowEdgeOverflow" : false});
        }
        {
            var Q0;
            Q0=makeQuery(id+"F1.opExtrude","CAP_EDGE",EDGE,{"disambiguationData":[OSD([sQuery(id+"F0.wireOp",EDGE,"E1.bottom")])],"isStart":false});
            fillet(context, id + "F15", {"entities" : qUnion([Q0]), "radius" : 2 * mm, "tangentPropagation" : true, "allowEdgeOverflow" : false});
        }
        {
            var Q0;
            {var subQ0=sQuery(id+"F0.wireOp",EDGE,"E21.filletArc");var subQ1=sQuery(id+"F0.wireOp",EDGE,"E7");var subQ2=sQuery(id+"F0.wireOp",EDGE,"E6");var subQ3=sQuery(id+"F0.wireOp",EDGE,"E5");var subQ4=sQuery(id+"F0.wireOp",EDGE,"E4");var subQ5=sQuery(id+"F0.wireOp",EDGE,"E22.filletArc");var subQ6=sQuery(id+"F0.wireOp",EDGE,"E1.bottom");var subQ7=sQuery(id+"F0.wireOp",EDGE,"E1.right");var subQ8=sQuery(id+"F0.wireOp",EDGE,"E1.top");var subQ9=sQuery(id+"F0.wireOp",EDGE,"E1.left");var subQ10=sQuery(id+"F0.wireOp",EDGE,"E23.filletArc");var subQ11=sQuery(id+"F0.wireOp",EDGE,"E24.filletArc");Q0=makeQuery(id+"F2.boolean.opBoolean","SPLIT",FACE,{"disambiguationData":[TD([makeQuery(id+"F1.opExtrude","SWEPT_FACE",FACE,{"disambiguationData":[OSD([subQ6])]})])],"derivedFrom":makeQuery(id+"F1.opExtrude","CAP_FACE",FACE,{"disambiguationData":[OSD([subQ6,subQ8,subQ9,subQ7,subQ4,subQ3,subQ2,subQ1,subQ0,subQ5,subQ10,subQ11])],"isStart":true})});}
            var sketch = newSketch(context, id + "F16", { "sketchPlane" : qUnion([Q0])});
            skLineSegment(sketch, "E79.0", {"start": v(-64.25, 80) * mm, "end": v(64.25, 80) * mm});
            skLineSegment(sketch, "E80", {"start": v(0, 80) * mm, "end": v(0, 152.2) * mm, "construction": true});
            skLineSegment(sketch, "E81", {"start": v(-33, 80) * mm, "end": v(-15, 98) * mm});
            skLineSegment(sketch, "E82", {"start": v(-15, 98) * mm, "end": v(-15, 110) * mm});
            skArc(sketch, "E83", {"start": v(15, 110) * mm, "mid": v(0, 125) * mm, "end": v(-15, 110) * mm});
            skLineSegment(sketch, "E84", {"start": v(15, 110) * mm, "end": v(15, 98) * mm});
            skLineSegment(sketch, "E85", {"start": v(15, 98) * mm, "end": v(33, 80) * mm});
            skCircle(sketch, "E86", {"center": v(0, 110) * mm, "radius": 6 * mm});
            skLineSegment(sketch, "E87", {"start": v(-90.9, 0) * mm, "end": v(103.56, 0) * mm, "construction": true});
            skLineSegment(sketch, "E88.MirrorCS", {"start": v(15, -98) * mm, "end": v(33, -80) * mm});
            skLineSegment(sketch, "E89.MirrorCS", {"start": v(15, -110) * mm, "end": v(15, -98) * mm});
            skArc(sketch, "E90.MirrorCS", {"start": v(15, -110) * mm, "mid": v(0, -125) * mm, "end": v(-15, -110) * mm});
            skLineSegment(sketch, "E91.MirrorCS", {"start": v(-15, -98) * mm, "end": v(-15, -110) * mm});
            skCircle(sketch, "E92.MirrorC", {"center": v(0, -110) * mm, "radius": 6 * mm});
            skLineSegment(sketch, "E93.MirrorCS", {"start": v(-33, -80) * mm, "end": v(-15, -98) * mm});
            skLineSegment(sketch, "E94.MirrorCS", {"start": v(0, -80) * mm, "end": v(0, -152.2) * mm, "construction": true});
            skLineSegment(sketch, "E95.MirrorCS", {"start": v(-64.25, -80) * mm, "end": v(64.25, -80) * mm});
            skLineSegment(sketch, "E96.0", {"start": v(-74.25, -70) * mm, "end": v(-74.25, 70) * mm});
            skArc(sketch, "E97.0", {"start": v(-64.25, 80) * mm, "mid": v(-71.32, 77.07) * mm, "end": v(-74.25, 70) * mm});
            skArc(sketch, "E98.0", {"start": v(-74.25, -70) * mm, "mid": v(-71.32, -77.07) * mm, "end": v(-64.25, -80) * mm});
            skArc(sketch, "E99.0", {"start": v(64.25, -80) * mm, "mid": v(71.32, -77.07) * mm, "end": v(74.25, -70) * mm});
            skLineSegment(sketch, "E100.0", {"start": v(74.25, -70) * mm, "end": v(74.25, 70) * mm});
            skArc(sketch, "E101.0", {"start": v(74.25, 70) * mm, "mid": v(71.32, 77.07) * mm, "end": v(64.25, 80) * mm});
            skArc(sketch, "E102.0", {"start": v(55.47, 48.14) * mm, "mid": v(0, 64.65) * mm, "end": v(-55.47, 48.14) * mm});
            skLineSegment(sketch, "E103.0", {"start": v(60, 39.77) * mm, "end": v(60, -39.77) * mm});
            skArc(sketch, "E104.0", {"start": v(60, 39.77) * mm, "mid": v(58.8, 44.53) * mm, "end": v(55.47, 48.14) * mm});
            skArc(sketch, "E105.0", {"start": v(-55.47, 48.14) * mm, "mid": v(-58.8, 44.53) * mm, "end": v(-60, 39.77) * mm});
            skLineSegment(sketch, "E106.0", {"start": v(-60, 39.77) * mm, "end": v(-60, -39.77) * mm});
            skArc(sketch, "E107.0", {"start": v(-60, -39.77) * mm, "mid": v(-58.8, -44.53) * mm, "end": v(-55.47, -48.14) * mm});
            skArc(sketch, "E108.0", {"start": v(-55.47, -48.14) * mm, "mid": v(0, -64.65) * mm, "end": v(55.47, -48.14) * mm});
            skCircle(sketch, "E109.0", {"center": v(60, -64.65) * mm, "radius": 4 * mm});
            skCircle(sketch, "E110.0", {"center": v(-60, -64.65) * mm, "radius": 4 * mm});
            skCircle(sketch, "E110.1", {"center": v(-60, 64.65) * mm, "radius": 4 * mm});
            skCircle(sketch, "E110.2", {"center": v(60, 64.65) * mm, "radius": 4 * mm});
            skArc(sketch, "E111.1", {"start": v(55.47, -48.14) * mm, "mid": v(58.8, -44.53) * mm, "end": v(60, -39.77) * mm});
            skSolve(sketch);
        }
        {
            var Q0;
            Q0=qSketchRegion(id+"F16",true);
            var Q1;
            Q1=makeQuery(id+"F2.opExtrude","CAP_FACE",FACE,{"disambiguationData":[OSD([sQuery(id+"F0.wireOp",EDGE,"E12"),sQuery(id+"F0.wireOp",EDGE,"E13"),sQuery(id+"F0.wireOp",EDGE,"E14"),sQuery(id+"F0.wireOp",EDGE,"E15"),sQuery(id+"F0.wireOp",EDGE,"E17.filletArc"),sQuery(id+"F0.wireOp",EDGE,"E18.filletArc"),sQuery(id+"F0.wireOp",EDGE,"E19.filletArc"),sQuery(id+"F0.wireOp",EDGE,"E20.filletArc"),sQuery(id+"F0.wireOp",EDGE,"E25.0"),sQuery(id+"F0.wireOp",EDGE,"E25.1"),sQuery(id+"F0.wireOp",EDGE,"E25.2"),sQuery(id+"F0.wireOp",EDGE,"E25.3"),sQuery(id+"F0.wireOp",EDGE,"E25.4"),sQuery(id+"F0.wireOp",EDGE,"E25.5"),sQuery(id+"F0.wireOp",EDGE,"E25.6"),sQuery(id+"F0.wireOp",EDGE,"E25.7")])],"isStart":false});
            extrude(context, id + "F17", {"entities" : qUnion([Q0]), "endBound" : BoundingType.UP_TO_SURFACE, "depth" : 25 * mm, "endBoundEntityFace" : qUnion([Q1]), "offsetDistance" : 25 * mm});
        }
    });
